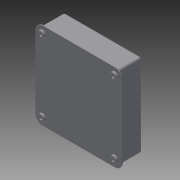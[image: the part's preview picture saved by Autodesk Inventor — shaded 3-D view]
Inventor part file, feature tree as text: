
AUTODESK INVENTOR PART (.ipt)
format: ipt  version: 2013 (Build 170138000, 138)  size: 299,520 bytes
history: native  units: mm
features: sketch x5, extrude x4, other x3, fillet x2, hole x1, chamfer x1
ambient origin geometry x8: Origin, YZ Plane, XZ Plane, XY Plane, X Axis, Y Axis, Z Axis, Center Point
feature tree (16):
  other  "ソリッド1"
  extrude  "押し出し1"  Depth=120.0mm
  extrude  "押し出し2"  Depth=120.0mm
  hole  "穴1"  [1 undecoded]
  fillet  "フィレット1"  Radius=60.0mm
  extrude  "押し出し3"  Depth=1.0mm TaperAngle=0.0deg
  fillet  "フィレット2"  Radius=4.0mm
  extrude  "押し出し4"  Depth=100.0mm
  chamfer  "面取り1"  Distance=100.0mm
  sketch  "スケッチ1"
  sketch  "スケッチ2"
  sketch  "スケッチ3"
  sketch  "スケッチ4"
  sketch  "スケッチ5"
  other  "断面エッジを投影1"
  other  "断面エッジを投影2"
note: 1 required parameter value undecoded (feature->parameter linkage not recoverable at this tier; creation-order binding heuristic only, values carry confidence <= 0.55)
